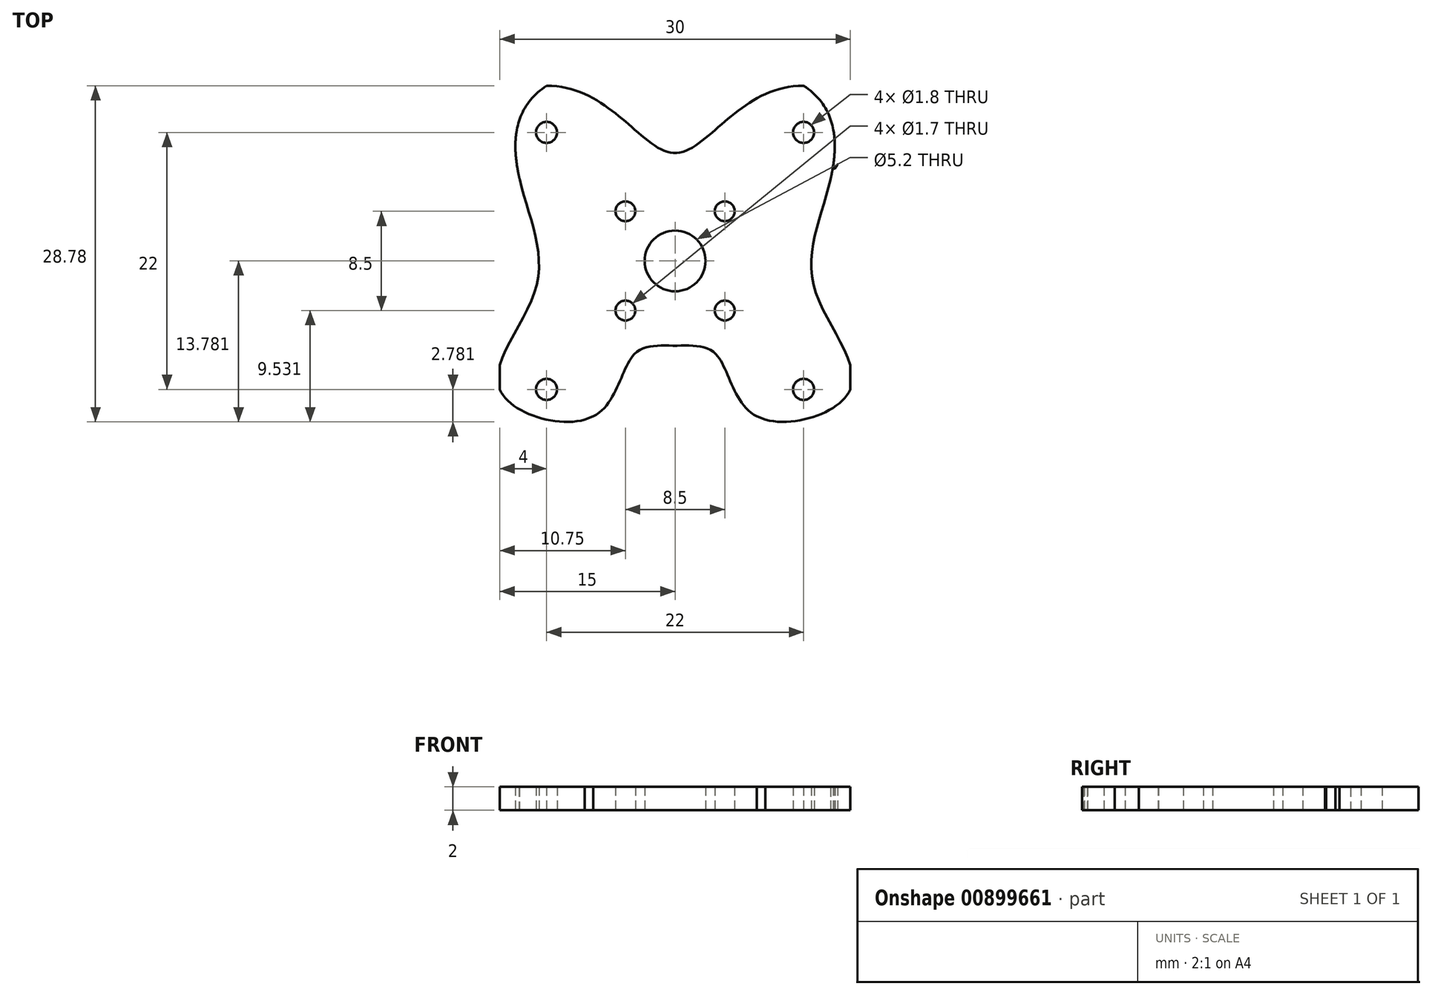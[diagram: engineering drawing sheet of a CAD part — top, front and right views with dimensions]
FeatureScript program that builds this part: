
annotation { "Feature Type Name" : "Feature", "Feature Type Description" : "" }
export const myFeature = defineFeature(function(context is Context, id is Id, definition is map)
    precondition{}
    {
        {
            var Q0;
            Q0=qCreatedBy(makeId("Top.planeOp"),FACE);
            var sketch = newSketch(context, id + "F0", { "sketchPlane" : qUnion([Q0])});
            skLineSegment(sketch, "E0", {"start": v(0, 13.68) * mm, "end": v(7.9, 0) * mm});
            skLineSegment(sketch, "E1", {"start": v(7.9, 0) * mm, "end": v(-7.9, 0) * mm});
            skLineSegment(sketch, "E2", {"start": v(-7.9, 0) * mm, "end": v(0, 13.68) * mm});
            skCircle(sketch, "E3", {"center": v(-7.9, 0) * mm, "radius": 1 * mm});
            skCircle(sketch, "E4", {"center": v(7.9, 0) * mm, "radius": 1 * mm});
            skCircle(sketch, "E5", {"center": v(0, 13.68) * mm, "radius": 1 * mm});
            skLineSegment(sketch, "E6", {"start": v(7.9, 0) * mm, "end": v(-3.95, 6.84) * mm});
            skLineSegment(sketch, "E7", {"start": v(-7.9, 0) * mm, "end": v(3.95, 6.84) * mm});
            skCircle(sketch, "E8", {"center": v(0, 4.56) * mm, "radius": 0.21 * mm});
            skLineSegment(sketch, "E9.bottom", {"start": v(-4.25, 8.81) * mm, "end": v(4.25, 8.81) * mm});
            skLineSegment(sketch, "E9.top", {"start": v(-4.25, 0.31) * mm, "end": v(4.25, 0.31) * mm});
            skLineSegment(sketch, "E9.left", {"start": v(-4.25, 8.81) * mm, "end": v(-4.25, 0.31) * mm});
            skLineSegment(sketch, "E9.right", {"start": v(4.25, 8.81) * mm, "end": v(4.25, 0.31) * mm});
            skCircle(sketch, "E10", {"center": v(-4.25, 8.81) * mm, "radius": 0.85 * mm});
            skCircle(sketch, "E11", {"center": v(4.25, 8.81) * mm, "radius": 0.85 * mm});
            skCircle(sketch, "E12", {"center": v(-4.25, 0.31) * mm, "radius": 0.85 * mm});
            skCircle(sketch, "E13", {"center": v(4.25, 0.31) * mm, "radius": 0.85 * mm});
            skLineSegment(sketch, "E14.bottom", {"start": v(15, 19.56) * mm, "end": v(-15, 19.56) * mm});
            skLineSegment(sketch, "E14.top", {"start": v(15, -10.44) * mm, "end": v(-15, -10.44) * mm});
            skLineSegment(sketch, "E14.left", {"start": v(15, 19.56) * mm, "end": v(15, -10.44) * mm});
            skLineSegment(sketch, "E14.right", {"start": v(-15, 19.56) * mm, "end": v(-15, -10.44) * mm});
            skLineSegment(sketch, "E15", {"start": v(-3.5, -10.44) * mm, "end": v(-3.5, -3.44) * mm});
            skLineSegment(sketch, "E16", {"start": v(-3.5, -3.44) * mm, "end": v(3.5, -3.44) * mm});
            skLineSegment(sketch, "E17", {"start": v(3.5, -3.44) * mm, "end": v(3.5, -10.44) * mm});
            skLineSegment(sketch, "E18.bottom", {"start": v(-11, 15.56) * mm, "end": v(11, 15.56) * mm});
            skLineSegment(sketch, "E18.top", {"start": v(-11, -6.44) * mm, "end": v(11, -6.44) * mm});
            skLineSegment(sketch, "E18.left", {"start": v(-11, 15.56) * mm, "end": v(-11, -6.44) * mm});
            skLineSegment(sketch, "E18.right", {"start": v(11, 15.56) * mm, "end": v(11, -6.44) * mm});
            skCircle(sketch, "E19", {"center": v(-11, 15.56) * mm, "radius": 0.9 * mm});
            skCircle(sketch, "E20", {"center": v(11, 15.56) * mm, "radius": 0.9 * mm});
            skCircle(sketch, "E21", {"center": v(-11, -6.44) * mm, "radius": 0.9 * mm});
            skCircle(sketch, "E22", {"center": v(11, -6.44) * mm, "radius": 0.9 * mm});
            skSolve(sketch);
        }
        {
            var Q0;
            Q0=qCreatedBy(makeId("Top.planeOp"),FACE);
            cPlane(context, id + "F1", {"entities" : qUnion([Q0]), "cplaneType" : CPlaneType.OFFSET, "offset" : 5 * mm, "width" : 150 * mm, "height" : 150 * mm});
        }
        {
            var Q0;
            Q0=qCreatedBy(id+"F1.planeOp",FACE);
            var sketch = newSketch(context, id + "F2", { "sketchPlane" : qUnion([Q0])});
            skPoint(sketch, "E23.0", {"position": v(0, 13.68) * mm});
            skCircle(sketch, "E24.0", {"center": v(4.25, 8.81) * mm, "radius": 0.85 * mm});
            skCircle(sketch, "E25.0", {"center": v(-4.25, 8.81) * mm, "radius": 0.85 * mm});
            skCircle(sketch, "E26.0", {"center": v(-7.9, 0) * mm, "radius": 1 * mm});
            skCircle(sketch, "E27.0", {"center": v(-4.25, 0.31) * mm, "radius": 0.85 * mm});
            skCircle(sketch, "E28.0", {"center": v(4.25, 0.31) * mm, "radius": 0.85 * mm});
            skCircle(sketch, "E29.0", {"center": v(7.9, 0) * mm, "radius": 1 * mm});
            skLineSegment(sketch, "E30.0", {"start": v(15, 19.56) * mm, "end": v(-15, 19.56) * mm});
            skLineSegment(sketch, "E31.0", {"start": v(-15, 19.56) * mm, "end": v(-15, -10.44) * mm});
            skLineSegment(sketch, "E32.0", {"start": v(-3.5, -10.44) * mm, "end": v(-3.5, -3.44) * mm});
            skLineSegment(sketch, "E33.0", {"start": v(-3.5, -3.44) * mm, "end": v(3.5, -3.44) * mm});
            skLineSegment(sketch, "E34.0", {"start": v(3.5, -3.44) * mm, "end": v(3.5, -10.44) * mm});
            skLineSegment(sketch, "E35.0", {"start": v(15, 19.56) * mm, "end": v(15, -10.44) * mm});
            skCircle(sketch, "E36", {"center": v(7.9, 0) * mm, "radius": 4 * mm});
            skCircle(sketch, "E37", {"center": v(-7.9, 0) * mm, "radius": 4 * mm});
            skPoint(sketch, "E38.0.midPoint", {"position": v(4, 13.68) * mm});
            skLineSegment(sketch, "E39.0", {"start": v(-3.9, 2.3) * mm, "end": v(-3.9, -2.3) * mm});
            skLineSegment(sketch, "E39.1", {"start": v(-3.9, -2.3) * mm, "end": v(-7.9, -4.62) * mm});
            skLineSegment(sketch, "E39.2", {"start": v(-7.9, -4.62) * mm, "end": v(-11.9, -2.3) * mm});
            skLineSegment(sketch, "E39.3", {"start": v(-11.9, -2.3) * mm, "end": v(-11.9, 2.3) * mm});
            skLineSegment(sketch, "E39.4", {"start": v(-11.9, 2.3) * mm, "end": v(-7.9, 4.62) * mm});
            skLineSegment(sketch, "E39.5", {"start": v(-7.9, 4.62) * mm, "end": v(-3.9, 2.3) * mm});
            skPoint(sketch, "E39.0.midPoint", {"position": v(-3.9, 0) * mm});
            skLineSegment(sketch, "E40.0", {"start": v(11.9, 2.3) * mm, "end": v(11.9, -2.3) * mm});
            skLineSegment(sketch, "E40.1", {"start": v(11.9, -2.3) * mm, "end": v(7.9, -4.62) * mm});
            skLineSegment(sketch, "E40.2", {"start": v(7.9, -4.62) * mm, "end": v(3.9, -2.3) * mm});
            skLineSegment(sketch, "E40.3", {"start": v(3.9, -2.3) * mm, "end": v(3.9, 2.3) * mm});
            skLineSegment(sketch, "E40.4", {"start": v(3.9, 2.3) * mm, "end": v(7.9, 4.62) * mm});
            skLineSegment(sketch, "E40.5", {"start": v(7.9, 4.62) * mm, "end": v(11.9, 2.3) * mm});
            skPoint(sketch, "E40.0.midPoint", {"position": v(11.9, 0) * mm});
            skLineSegment(sketch, "E41.bottom", {"start": v(-4.25, 8.81) * mm, "end": v(-9.25, 8.81) * mm});
            skLineSegment(sketch, "E41.top", {"start": v(-4.25, 13.81) * mm, "end": v(-9.25, 13.81) * mm});
            skLineSegment(sketch, "E41.left", {"start": v(-4.25, 8.81) * mm, "end": v(-4.25, 13.81) * mm});
            skLineSegment(sketch, "E41.right", {"start": v(-9.25, 8.81) * mm, "end": v(-9.25, 13.81) * mm});
            skLineSegment(sketch, "E42.bottom", {"start": v(4.25, 8.81) * mm, "end": v(9.25, 8.81) * mm});
            skLineSegment(sketch, "E42.top", {"start": v(4.25, 13.81) * mm, "end": v(9.25, 13.81) * mm});
            skLineSegment(sketch, "E42.left", {"start": v(4.25, 8.81) * mm, "end": v(4.25, 13.81) * mm});
            skLineSegment(sketch, "E42.right", {"start": v(9.25, 8.81) * mm, "end": v(9.25, 13.81) * mm});
            skLineSegment(sketch, "E43.bottom", {"start": v(-4.25, 0.31) * mm, "end": v(-9.25, 0.31) * mm});
            skLineSegment(sketch, "E43.top", {"start": v(-4.25, -4.69) * mm, "end": v(-9.25, -4.69) * mm});
            skLineSegment(sketch, "E43.left", {"start": v(-4.25, 0.31) * mm, "end": v(-4.25, -4.69) * mm});
            skLineSegment(sketch, "E43.right", {"start": v(-9.25, 0.31) * mm, "end": v(-9.25, -4.69) * mm});
            skLineSegment(sketch, "E44.bottom", {"start": v(4.25, 0.31) * mm, "end": v(9.25, 0.31) * mm});
            skLineSegment(sketch, "E44.top", {"start": v(4.25, -4.69) * mm, "end": v(9.25, -4.69) * mm});
            skLineSegment(sketch, "E44.left", {"start": v(4.25, 0.31) * mm, "end": v(4.25, -4.69) * mm});
            skLineSegment(sketch, "E44.right", {"start": v(9.25, 0.31) * mm, "end": v(9.25, -4.69) * mm});
            skFitSpline(sketch, "E45", {"points": [v(0, 18.3) * mm, v(-9.25, 13.81) * mm, v(-11.9, 2.3) * mm, v(-11.9, -2.3) * mm, v(-9.25, -4.69) * mm, v(-4.25, -4.69) * mm, v(-3.5, -3.44) * mm, v(0, -2.3) * mm, v(3.5, -3.44) * mm, v(4.25, -4.69) * mm, v(9.25, -4.69) * mm, v(11.9, -2.3) * mm, v(11.9, 2.3) * mm, v(9.25, 13.81) * mm, v(0, 18.3) * mm]});
            skCircle(sketch, "E46.0", {"center": v(-11, 15.56) * mm, "radius": 0.9 * mm});
            skCircle(sketch, "E47.0", {"center": v(11, 15.56) * mm, "radius": 0.9 * mm});
            skCircle(sketch, "E48.0", {"center": v(11, -6.44) * mm, "radius": 0.9 * mm});
            skCircle(sketch, "E49.0", {"center": v(-11, -6.44) * mm, "radius": 0.9 * mm});
            skCircle(sketch, "E50.cCircle", {"center": v(-11, 15.56) * mm, "radius": 4 * mm, "construction": true});
            skLineSegment(sketch, "E50.0", {"start": v(-13.3, 19.56) * mm, "end": v(-8.7, 19.56) * mm});
            skLineSegment(sketch, "E50.1", {"start": v(-8.7, 19.56) * mm, "end": v(-6.38, 15.56) * mm});
            skLineSegment(sketch, "E50.2", {"start": v(-6.38, 15.56) * mm, "end": v(-8.7, 11.56) * mm});
            skLineSegment(sketch, "E50.3", {"start": v(-8.7, 11.56) * mm, "end": v(-13.3, 11.56) * mm});
            skLineSegment(sketch, "E50.4", {"start": v(-13.3, 11.56) * mm, "end": v(-15.62, 15.56) * mm});
            skLineSegment(sketch, "E50.5", {"start": v(-15.62, 15.56) * mm, "end": v(-13.3, 19.56) * mm});
            skPoint(sketch, "E50.0.midPoint", {"position": v(-11, 19.56) * mm});
            skCircle(sketch, "E51.cCircle", {"center": v(11, 15.56) * mm, "radius": 4 * mm, "construction": true});
            skLineSegment(sketch, "E51.0", {"start": v(8.7, 19.56) * mm, "end": v(13.3, 19.56) * mm});
            skLineSegment(sketch, "E51.1", {"start": v(13.3, 19.56) * mm, "end": v(15.62, 15.56) * mm});
            skLineSegment(sketch, "E51.2", {"start": v(15.62, 15.56) * mm, "end": v(13.3, 11.56) * mm});
            skLineSegment(sketch, "E51.3", {"start": v(13.3, 11.56) * mm, "end": v(8.7, 11.56) * mm});
            skLineSegment(sketch, "E51.4", {"start": v(8.7, 11.56) * mm, "end": v(6.38, 15.56) * mm});
            skLineSegment(sketch, "E51.5", {"start": v(6.38, 15.56) * mm, "end": v(8.7, 19.56) * mm});
            skPoint(sketch, "E51.0.midPoint", {"position": v(11, 19.56) * mm});
            skCircle(sketch, "E52.cCircle", {"center": v(11, -6.44) * mm, "radius": 4 * mm, "construction": true});
            skLineSegment(sketch, "E52.0", {"start": v(15, -4.13) * mm, "end": v(15, -8.75) * mm});
            skLineSegment(sketch, "E52.1", {"start": v(15, -8.75) * mm, "end": v(11, -11.06) * mm});
            skLineSegment(sketch, "E52.2", {"start": v(11, -11.06) * mm, "end": v(7, -8.75) * mm});
            skLineSegment(sketch, "E52.3", {"start": v(7, -8.75) * mm, "end": v(7, -4.13) * mm});
            skLineSegment(sketch, "E52.4", {"start": v(7, -4.13) * mm, "end": v(11, -1.82) * mm});
            skLineSegment(sketch, "E52.5", {"start": v(11, -1.82) * mm, "end": v(15, -4.13) * mm});
            skPoint(sketch, "E52.0.midPoint", {"position": v(15, -6.44) * mm});
            skCircle(sketch, "E53.cCircle", {"center": v(-11, -6.44) * mm, "radius": 4 * mm, "construction": true});
            skLineSegment(sketch, "E53.0", {"start": v(-15, -8.75) * mm, "end": v(-15, -4.13) * mm});
            skLineSegment(sketch, "E53.1", {"start": v(-15, -4.13) * mm, "end": v(-11, -1.82) * mm});
            skLineSegment(sketch, "E53.2", {"start": v(-11, -1.82) * mm, "end": v(-7, -4.13) * mm});
            skLineSegment(sketch, "E53.3", {"start": v(-7, -4.13) * mm, "end": v(-7, -8.75) * mm});
            skLineSegment(sketch, "E53.4", {"start": v(-7, -8.75) * mm, "end": v(-11, -11.06) * mm});
            skLineSegment(sketch, "E53.5", {"start": v(-11, -11.06) * mm, "end": v(-15, -8.75) * mm});
            skPoint(sketch, "E53.0.midPoint", {"position": v(-15, -6.44) * mm});
            skLineSegment(sketch, "E54", {"start": v(-15, -10.44) * mm, "end": v(-3.5, -10.44) * mm});
            skLineSegment(sketch, "E55", {"start": v(3.5, -10.44) * mm, "end": v(15, -10.44) * mm});
            skSolve(sketch);
        }
        {
            var Q0;
            Q0=qCreatedBy(id+"F1.planeOp",FACE);
            var sketch = newSketch(context, id + "F3", { "sketchPlane" : qUnion([Q0])});
            skLineSegment(sketch, "E56.0", {"start": v(15, 19.56) * mm, "end": v(-15, 19.56) * mm});
            skLineSegment(sketch, "E57.0", {"start": v(-15, 19.56) * mm, "end": v(-15, -10.44) * mm});
            skLineSegment(sketch, "E58.0", {"start": v(15, 19.56) * mm, "end": v(15, -10.44) * mm});
            skLineSegment(sketch, "E59.0", {"start": v(15, -10.44) * mm, "end": v(-15, -10.44) * mm});
            skLineSegment(sketch, "E60.0", {"start": v(3.5, -3.44) * mm, "end": v(3.5, -10.44) * mm});
            skLineSegment(sketch, "E61.0", {"start": v(-3.5, -3.44) * mm, "end": v(3.5, -3.44) * mm});
            skLineSegment(sketch, "E62.0", {"start": v(-3.5, -10.44) * mm, "end": v(-3.5, -3.44) * mm});
            skCircle(sketch, "E63.0", {"center": v(-11, -6.44) * mm, "radius": 0.9 * mm});
            skCircle(sketch, "E64.0", {"center": v(11, -6.44) * mm, "radius": 0.9 * mm});
            skCircle(sketch, "E65.0", {"center": v(4.25, 0.31) * mm, "radius": 0.85 * mm});
            skCircle(sketch, "E66.0", {"center": v(-4.25, 0.31) * mm, "radius": 0.85 * mm});
            skCircle(sketch, "E67.0", {"center": v(-4.25, 8.81) * mm, "radius": 0.85 * mm});
            skCircle(sketch, "E68.0", {"center": v(4.25, 8.81) * mm, "radius": 0.85 * mm});
            skCircle(sketch, "E69.0", {"center": v(-11, 15.56) * mm, "radius": 0.9 * mm});
            skCircle(sketch, "E70.0", {"center": v(11, 15.56) * mm, "radius": 0.9 * mm});
            skCircle(sketch, "E71.0", {"center": v(11, 15.56) * mm, "radius": 4 * mm});
            skLineSegment(sketch, "E72.0", {"start": v(11, -11.06) * mm, "end": v(7, -8.75) * mm});
            skLineSegment(sketch, "E73.0", {"start": v(-7, -8.75) * mm, "end": v(-11, -11.06) * mm});
            skPoint(sketch, "E74.0", {"position": v(15, -6.44) * mm});
            skPoint(sketch, "E75.0", {"position": v(-15, -6.44) * mm});
            skPoint(sketch, "E76.0", {"position": v(-11, 19.56) * mm});
            skPoint(sketch, "E77.0", {"position": v(11, 19.56) * mm});
            skPoint(sketch, "E78.0", {"position": v(13.3, 11.56) * mm});
            skPoint(sketch, "E79.0", {"position": v(-13.3, 11.56) * mm});
            skPoint(sketch, "E80.0", {"position": v(-11.9, 2.3) * mm});
            skPoint(sketch, "E81.0", {"position": v(11.9, 2.3) * mm});
            skFitSpline(sketch, "E82", {"points": [v(-13.3, 11.56) * mm, v(-11.9, 2.3) * mm, v(-15, -6.44) * mm, v(-7, -8.75) * mm, v(-3.5, -3.44) * mm, v(0, -2.7) * mm, v(3.5, -3.44) * mm, v(7, -8.75) * mm, v(15, -6.44) * mm, v(11.9, 2.3) * mm, v(13.3, 11.56) * mm, v(11, 19.56) * mm, v(-11, 19.56) * mm, v(-13.3, 11.56) * mm]});
            skLineSegment(sketch, "E83", {"start": v(-11, 19.56) * mm, "end": v(11, 19.56) * mm});
            skPoint(sketch, "E84.0", {"position": v(-15.62, 15.56) * mm});
            skPoint(sketch, "E85.0", {"position": v(15.62, 15.56) * mm});
            skLineSegment(sketch, "E86", {"start": v(-15.62, 15.56) * mm, "end": v(15.62, 15.56) * mm});
            skFitSpline(sketch, "E87", {"points": [v(-13.3, 11.56) * mm, v(-15, 15.56) * mm, v(-11, 19.56) * mm], "startDerivative": vector(-1.03, 5.82) * mm, "endDerivative": vector(12.95, 0) * mm});
            skFitSpline(sketch, "E88", {"points": [v(13.3, 11.56) * mm, v(15, 15.56) * mm, v(11, 19.56) * mm], "startDerivative": vector(1.03, 5.82) * mm, "endDerivative": vector(-12.95, 0) * mm});
            skFitSpline(sketch, "E89", {"points": [v(-15, -6.44) * mm, v(-12.94, -9.98) * mm, v(-7, -8.75) * mm], "startDerivative": vector(3, -9.98) * mm, "endDerivative": vector(12.57, 4.87) * mm});
            skFitSpline(sketch, "E90", {"points": [v(15, -6.44) * mm, v(12.94, -9.93) * mm, v(7, -8.75) * mm], "startDerivative": vector(-3, -10) * mm, "endDerivative": vector(-12.54, 4.86) * mm});
            skPoint(sketch, "E91.0", {"position": v(0, 4.56) * mm});
            skCircle(sketch, "E92", {"center": v(0, 4.56) * mm, "radius": 2.6 * mm});
            skPoint(sketch, "E93.0", {"position": v(0, 18.3) * mm});
            skPoint(sketch, "E94.1.internal.snap0", {"position": v(0, 15.56) * mm});
            skFitSpline(sketch, "E94", {"points": [v(-11, 19.56) * mm, v(0, 13.78) * mm, v(11, 19.56) * mm], "startDerivative": vector(33, 0) * mm, "endDerivative": vector(33, 0) * mm});
            skLineSegment(sketch, "E95", {"start": v(-15, 12.47) * mm, "end": v(15, 12.47) * mm});
            skLineSegment(sketch, "E96", {"start": v(-13.3, 11.56) * mm, "end": v(-13.47, 12.47) * mm});
            skLineSegment(sketch, "E97", {"start": v(13.3, 11.56) * mm, "end": v(13.47, 12.47) * mm});
            skSolve(sketch);
        }
        {
            var Q0;
            Q0=makeQuery(id+"F3.imprint","IMPRINT",FACE,{"disambiguationData":[TD([[makeQuery(id+"F3.imprint","IMPRINT",EDGE,{"derivedFrom":sQuery(id+"F3.wireOp",EDGE,"E63.0")}),-1.0]])]});
            var Q1;
            {var subQ0=sQuery(id+"F3.wireOp",EDGE,"E86");var subQ1=sQuery(id+"F3.wireOp",EDGE,"E70.0");var subQ8=makeQuery(id+"F3.imprint","INTERSECT",VERTEX,{"disambiguationData":[OD(0.0)],"derivedFrom":[subQ1,subQ0]});Q1=makeQuery(id+"F3.imprint","IMPRINT",FACE,{"disambiguationData":[TD([[makeQuery(id+"F3.imprint","IMPRINT",EDGE,{"disambiguationData":[TD([[subQ8,-1.0]])],"derivedFrom":subQ1}),-1.0]])]});}
            var Q2;
            {var subQ0=sQuery(id+"F3.wireOp",EDGE,"E86");var subQ1=sQuery(id+"F3.wireOp",EDGE,"E70.0");var subQ2=makeQuery(id+"F3.imprint","INTERSECT",VERTEX,{"disambiguationData":[OD(0.0)],"derivedFrom":[subQ1,subQ0]});Q2=makeQuery(id+"F3.imprint","IMPRINT",FACE,{"disambiguationData":[TD([[makeQuery(id+"F3.imprint","IMPRINT",EDGE,{"disambiguationData":[TD([[subQ2,1.0]])],"derivedFrom":subQ1}),-1.0]])]});}
            var Q3;
            {var subQ1=sQuery(id+"F3.wireOp",EDGE,"E71.0");var subQ3=sQuery(id+"F3.wireOp",EDGE,"E86");var subQ4=makeQuery(id+"F3.imprint","INTERSECT",VERTEX,{"derivedFrom":[subQ1,subQ3]});Q3=makeQuery(id+"F3.imprint","IMPRINT",FACE,{"disambiguationData":[TD([[makeQuery(id+"F3.imprint","IMPRINT",EDGE,{"disambiguationData":[TD([[subQ4,1.0]])],"derivedFrom":subQ3}),1.0]])]});}
            var Q4;
            {var subQ1=sQuery(id+"F3.wireOp",EDGE,"E86");var subQ4=sQuery(id+"F3.wireOp",EDGE,"E69.0");var subQ5=makeQuery(id+"F3.imprint","INTERSECT",VERTEX,{"disambiguationData":[OD(0.0)],"derivedFrom":[subQ4,subQ1]});Q4=makeQuery(id+"F3.imprint","IMPRINT",FACE,{"disambiguationData":[TD([[makeQuery(id+"F3.imprint","IMPRINT",EDGE,{"disambiguationData":[TD([[subQ5,1.0]])],"derivedFrom":subQ4}),-1.0]])]});}
            var Q5;
            {var subQ0=sQuery(id+"F3.wireOp",EDGE,"E95");var subQ1=sQuery(id+"F3.wireOp",EDGE,"E71.0");var subQ2=makeQuery(id+"F3.imprint","INTERSECT",VERTEX,{"disambiguationData":[OD(0.0)],"derivedFrom":[subQ1,subQ0]});Q5=makeQuery(id+"F3.imprint","IMPRINT",FACE,{"disambiguationData":[TD([[makeQuery(id+"F3.imprint","IMPRINT",EDGE,{"disambiguationData":[TD([[subQ2,-1.0]])],"derivedFrom":subQ1}),1.0]])]});}
            var Q6;
            {var subQ0=sQuery(id+"F3.wireOp",EDGE,"E86");var subQ1=sQuery(id+"F3.wireOp",EDGE,"E69.0");var subQ11=makeQuery(id+"F3.imprint","INTERSECT",VERTEX,{"disambiguationData":[OD(0.0)],"derivedFrom":[subQ1,subQ0]});Q6=makeQuery(id+"F3.imprint","IMPRINT",FACE,{"disambiguationData":[TD([[makeQuery(id+"F3.imprint","IMPRINT",EDGE,{"disambiguationData":[TD([[subQ11,-1.0]])],"derivedFrom":subQ1}),-1.0]])]});}
            var Q7;
            {var subQ0=sQuery(id+"F3.wireOp",EDGE,"E96");Q7=makeQuery(id+"F3.imprint","IMPRINT",FACE,{"disambiguationData":[TD([[makeQuery(id+"F3.imprint","IMPRINT",EDGE,{"derivedFrom":subQ0}),1.0]])]});}
            var Q8;
            {var subQ0=sQuery(id+"F3.wireOp",EDGE,"E97");var subQ1=sQuery(id+"F3.wireOp",EDGE,"E71.0");var subQ2=makeQuery(id+"F3.imprint","INTERSECT",VERTEX,{"derivedFrom":[subQ1,subQ0]});Q8=makeQuery(id+"F3.imprint","IMPRINT",FACE,{"disambiguationData":[TD([[makeQuery(id+"F3.imprint","IMPRINT",EDGE,{"disambiguationData":[TD([[subQ2,-1.0]])],"derivedFrom":subQ1}),-1.0]])]});}
            var Q9;
            {var subQ0=sQuery(id+"F3.wireOp",EDGE,"E95");var subQ1=sQuery(id+"F3.wireOp",EDGE,"E71.0");var subQ2=makeQuery(id+"F3.imprint","INTERSECT",VERTEX,{"disambiguationData":[OD(1.0)],"derivedFrom":[subQ1,subQ0]});Q9=makeQuery(id+"F3.imprint","IMPRINT",FACE,{"disambiguationData":[TD([[makeQuery(id+"F3.imprint","IMPRINT",EDGE,{"disambiguationData":[TD([[subQ2,-1.0]])],"derivedFrom":subQ1}),-1.0]])]});}
            var Q10;
            {var subQ0=sQuery(id+"F3.wireOp",EDGE,"E97");var subQ1=sQuery(id+"F3.wireOp",EDGE,"E71.0");var subQ2=makeQuery(id+"F3.imprint","INTERSECT",VERTEX,{"derivedFrom":[subQ1,subQ0]});Q10=makeQuery(id+"F3.imprint","IMPRINT",FACE,{"disambiguationData":[TD([[makeQuery(id+"F3.imprint","IMPRINT",EDGE,{"disambiguationData":[TD([[subQ2,-1.0]])],"derivedFrom":subQ1}),1.0]])]});}
            extrude(context, id + "F4", {"entities" : qUnion([Q0, Q1, Q2, Q3, Q4, Q5, Q6, Q7, Q8, Q9, Q10]), "depth" : 2 * mm, "offsetDistance" : 25 * mm});
        }
    });
